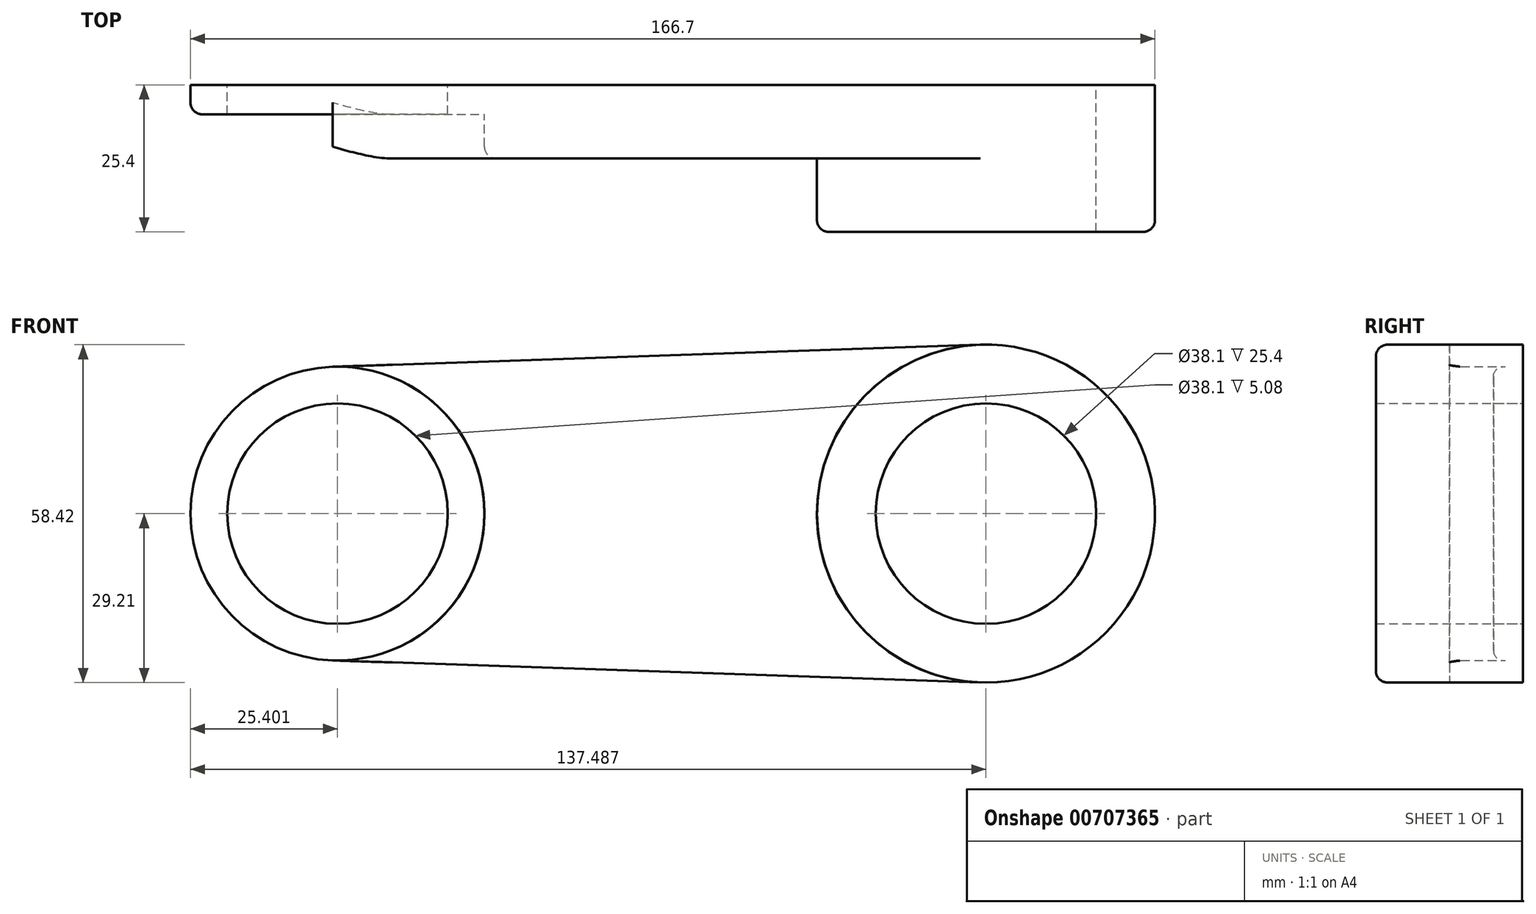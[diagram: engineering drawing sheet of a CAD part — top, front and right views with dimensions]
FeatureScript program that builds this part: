
annotation { "Feature Type Name" : "Feature", "Feature Type Description" : "" }
export const myFeature = defineFeature(function(context is Context, id is Id, definition is map)
    precondition{}
    {
        {
            var Q0;
            Q0=qCreatedBy(makeId("Front.planeOp"),FACE);
            var sketch = newSketch(context, id + "F0", { "sketchPlane" : qUnion([Q0])});
            skCircle(sketch, "E0", {"center": v(-68.28, 0) * mm, "radius": 25.4 * mm});
            skCircle(sketch, "E1", {"center": v(-68.28, 0) * mm, "radius": 19.05 * mm});
            skCircle(sketch, "E2", {"center": v(43.8, 0) * mm, "radius": 29.21 * mm});
            skCircle(sketch, "E3", {"center": v(43.8, 0) * mm, "radius": 19.05 * mm});
            skLineSegment(sketch, "E4", {"start": v(-69.14, 25.39) * mm, "end": v(42.81, 29.2) * mm});
            skLineSegment(sketch, "E5", {"start": v(-69.14, -25.39) * mm, "end": v(42.81, -29.2) * mm});
            skSolve(sketch);
        }
        {
            var Q0;
            Q0=makeQuery(id+"F0.imprint","IMPRINT",FACE,{"disambiguationData":[TD([[makeQuery(id+"F0.imprint","IMPRINT",EDGE,{"derivedFrom":sQuery(id+"F0.wireOp",EDGE,"E3")}),-1.0]])]});
            extrude(context, id + "F1", {"entities" : qUnion([Q0]), "depth" : 25.4 * mm, "offsetDistance" : 25.4 * mm});
        }
        {
            var Q0;
            {var subQ0=sQuery(id+"F0.wireOp",EDGE,"E4");Q0=makeQuery(id+"F0.imprint","IMPRINT",FACE,{"disambiguationData":[TD([[makeQuery(id+"F0.imprint","IMPRINT",EDGE,{"derivedFrom":subQ0}),-1.0]])]});}
            extrude(context, id + "F2", {"entities" : qUnion([Q0]), "operationType" : NewBodyOperationType.ADD, "depth" : 12.7 * mm, "offsetDistance" : 25.4 * mm});
        }
        {
            var Q0;
            Q0=makeQuery(id+"F0.imprint","IMPRINT",FACE,{"disambiguationData":[TD([[makeQuery(id+"F0.imprint","IMPRINT",EDGE,{"derivedFrom":sQuery(id+"F0.wireOp",EDGE,"E1")}),-1.0]])]});
            extrude(context, id + "F3", {"entities" : qUnion([Q0]), "operationType" : NewBodyOperationType.ADD, "depth" : 5.08 * mm, "offsetDistance" : 25.4 * mm});
        }
        {
            var Q0;
            Q0=makeQuery(id+"F1.opExtrude","CAP_EDGE",EDGE,{"disambiguationData":[OSD([sQuery(id+"F0.wireOp",EDGE,"E2")])],"isStart":false});
            var Q1;
            {var subQ0=sQuery(id+"F0.wireOp",EDGE,"E0");Q1=makeQuery(id+"F3.boolean.opBoolean","SPLIT",EDGE,{"disambiguationData":[topologyDisambiguationEdgeConnected([makeQuery(id+"F3.opExtrude","SWEPT_FACE",FACE,{"disambiguationData":[OSD([subQ0])]})])],"derivedFrom":makeQuery(id+"F3.opExtrude","CAP_EDGE",EDGE,{"disambiguationData":[OSD([subQ0])],"isStart":false})});}
            var Q2;
            Q2=makeQuery(id+"F2.opExtrude","CAP_EDGE",EDGE,{"disambiguationData":[OSD([sQuery(id+"F0.wireOp",EDGE,"E0")])],"isStart":false});
            var Q3;
            Q3=makeQuery(id+"F2.opExtrude","CAP_EDGE",EDGE,{"disambiguationData":[OSD([sQuery(id+"F0.wireOp",EDGE,"E2")])],"isStart":false});
            fillet(context, id + "F4", {"entities" : qUnion([Q0, Q1, Q2, Q3]), "radius" : 2.03 * mm, "tangentPropagation" : true, "allowEdgeOverflow" : false});
        }
    });
